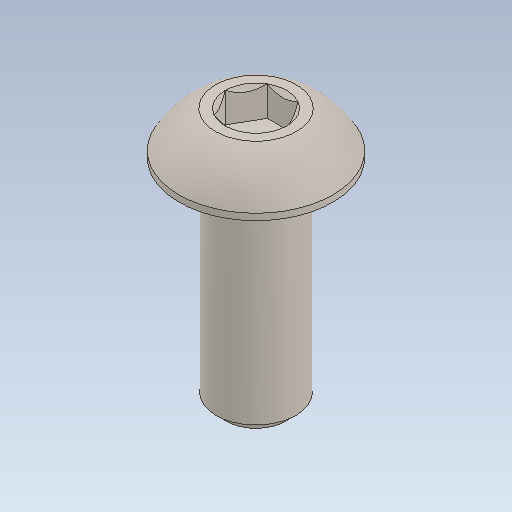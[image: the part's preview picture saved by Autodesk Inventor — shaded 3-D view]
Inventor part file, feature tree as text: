
AUTODESK INVENTOR PART (.ipt)
format: ipt  version: 2020 (Build 240168000, 168)  size: 131,072 bytes
history: native  units: in
note: dims shown in document units (in); Inventor stores cm internally (conversion verified against a paired STEP export)
features: fillet x1
ambient origin geometry x8: Origin, YZ Plane, XZ Plane, XY Plane, X Axis, Y Axis, Z Axis, Center Point
bodies: Solid1 (feature_tree)
feature tree (1):
  fillet  "Fillet1"  [1 undecoded]
note: 1 required parameter value undecoded (feature->parameter linkage not recoverable at this tier; creation-order binding heuristic only, values carry confidence <= 0.55)
